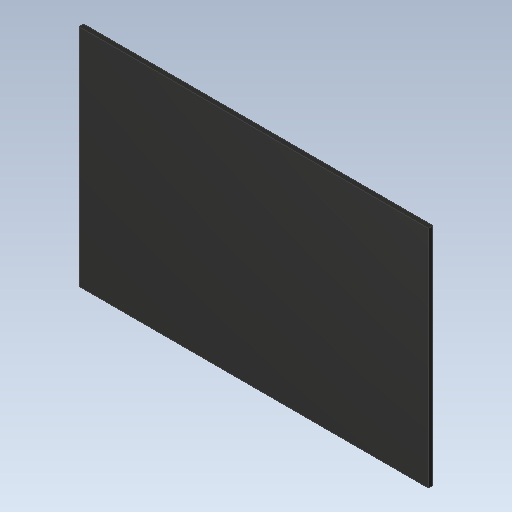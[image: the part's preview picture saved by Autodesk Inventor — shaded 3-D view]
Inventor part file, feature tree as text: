
AUTODESK INVENTOR PART (.ipt)
format: ipt  version: 2023 (Build 270158000, 158)  size: 91,136 bytes
history: imported  units: in
note: dims shown in document units (in); Inventor stores cm internally (conversion verified against a paired STEP export)
features: imported_body x1
ambient origin geometry x8: Origin, YZ Plane, XZ Plane, XY Plane, X Axis, Y Axis, Z Axis, Center Point
bodies: Solid1 (imported_parasolid), Body1 (imported_parasolid)
feature tree (1):
  imported_body  NMx_Import_Brep_tag  [imported B-rep: ~6 faces, bbox_mm=[7.6952, 4.953, 0.1]]
